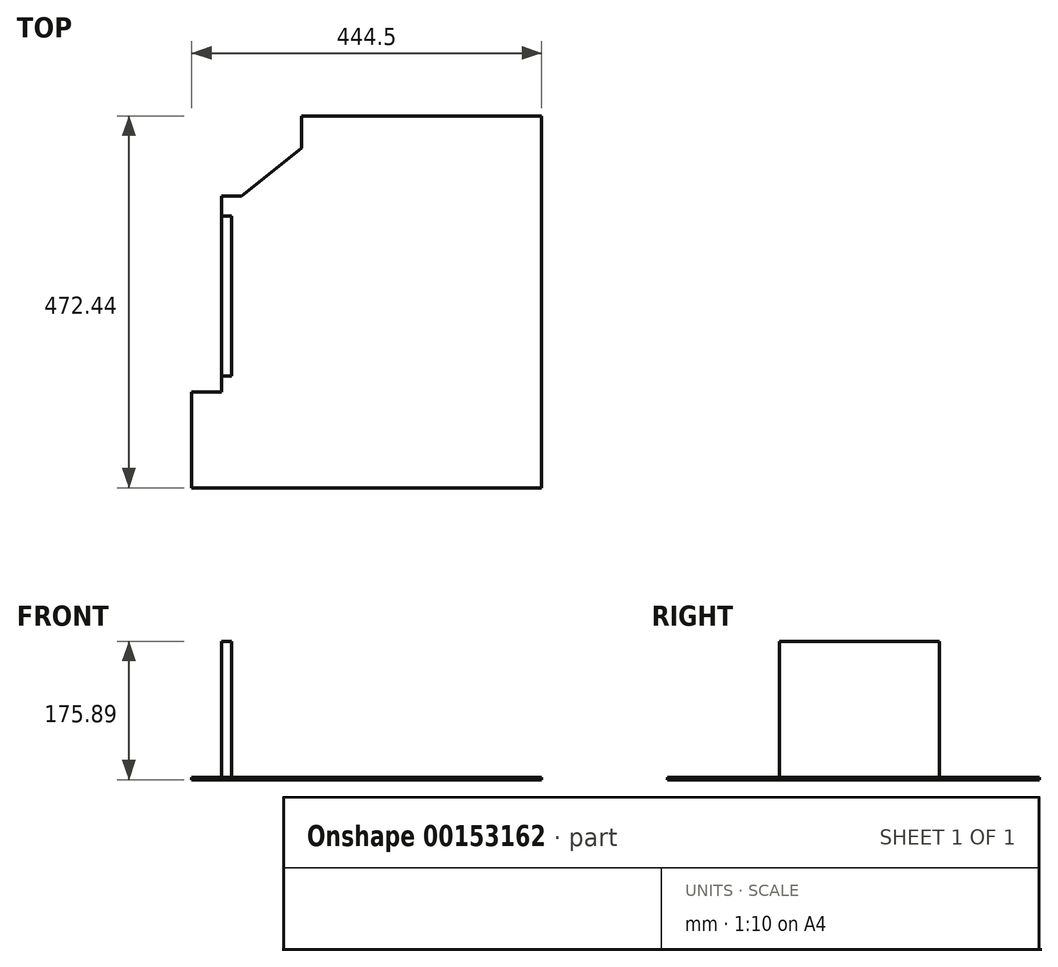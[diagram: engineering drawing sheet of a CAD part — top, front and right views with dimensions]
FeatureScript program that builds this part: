
annotation { "Feature Type Name" : "Feature", "Feature Type Description" : "" }
export const myFeature = defineFeature(function(context is Context, id is Id, definition is map)
    precondition{}
    {
        {
            var Q0;
            Q0=qCreatedBy(makeId("Top.planeOp"),FACE);
            var sketch = newSketch(context, id + "F0", { "sketchPlane" : qUnion([Q0])});
            skLineSegment(sketch, "E0", {"start": v(196.15, -173.15) * mm, "end": v(196.15, 299.29) * mm});
            skLineSegment(sketch, "E1", {"start": v(196.15, 299.29) * mm, "end": v(-108.65, 299.29) * mm});
            skLineSegment(sketch, "E2", {"start": v(-108.65, 299.29) * mm, "end": v(-108.65, 258.65) * mm});
            skLineSegment(sketch, "E3", {"start": v(-108.65, 258.65) * mm, "end": v(-184.85, 197.37) * mm});
            skLineSegment(sketch, "E4", {"start": v(-184.85, 197.69) * mm, "end": v(-184.85, 197.37) * mm});
            skLineSegment(sketch, "E5", {"start": v(-184.85, 197.69) * mm, "end": v(-210.25, 197.69) * mm});
            skLineSegment(sketch, "E6", {"start": v(-210.25, 197.69) * mm, "end": v(-210.25, -173.15) * mm});
            skLineSegment(sketch, "E7", {"start": v(-210.25, -173.15) * mm, "end": v(196.15, -173.15) * mm});
            skLineSegment(sketch, "E8.bottom", {"start": v(-210.25, -173.15) * mm, "end": v(-248.35, -173.15) * mm});
            skLineSegment(sketch, "E8.top", {"start": v(-210.25, -51.23) * mm, "end": v(-248.35, -51.23) * mm});
            skLineSegment(sketch, "E8.left", {"start": v(-210.25, -173.15) * mm, "end": v(-210.25, -51.23) * mm});
            skLineSegment(sketch, "E8.right", {"start": v(-248.35, -173.15) * mm, "end": v(-248.35, -51.23) * mm});
            skLineSegment(sketch, "E9.bottom", {"start": v(-210.25, -28.53) * mm, "end": v(-197.55, -28.53) * mm});
            skLineSegment(sketch, "E9.top", {"start": v(-210.25, 149.27) * mm, "end": v(-197.55, 149.27) * mm});
            skLineSegment(sketch, "E9.left", {"start": v(-210.25, -28.53) * mm, "end": v(-210.25, 149.27) * mm});
            skLineSegment(sketch, "E9.right", {"start": v(-197.55, -28.53) * mm, "end": v(-197.55, 149.27) * mm});
            skSolve(sketch);
        }
        {
            var Q0;
            Q0 = qSketchRegion(id + "F0", true);
            extrude(context, id + "F1", {"entities" : qUnion([Q0]), "depth" : 3.17 * mm});
        }
        {
            var Q0;
            Q0=makeQuery(id+"F1.opExtrude","CAP_FACE",FACE,{"disambiguationData":[OSD([sQuery(id+"F0.wireOp",EDGE,"E0"),sQuery(id+"F0.wireOp",EDGE,"E1"),sQuery(id+"F0.wireOp",EDGE,"E2"),sQuery(id+"F0.wireOp",EDGE,"E3"),sQuery(id+"F0.wireOp",EDGE,"E4"),sQuery(id+"F0.wireOp",EDGE,"E5"),sQuery(id+"F0.wireOp",EDGE,"E6"),sQuery(id+"F0.wireOp",EDGE,"E7"),sQuery(id+"F0.wireOp",EDGE,"E8.bottom"),sQuery(id+"F0.wireOp",EDGE,"E8.top"),sQuery(id+"F0.wireOp",EDGE,"E8.right"),sQuery(id+"F0.wireOp",EDGE,"E9.left")])],"isStart":false});
            var sketch = newSketch(context, id + "F2", { "sketchPlane" : qUnion([Q0])});
            skLineSegment(sketch, "E10.bottom", {"start": v(-210.25, -31.2) * mm, "end": v(-197.55, -31.2) * mm});
            skLineSegment(sketch, "E10.top", {"start": v(-210.25, 172.29) * mm, "end": v(-197.55, 172.29) * mm});
            skLineSegment(sketch, "E10.left", {"start": v(-210.25, -31.2) * mm, "end": v(-210.25, 172.29) * mm});
            skLineSegment(sketch, "E10.right", {"start": v(-197.55, -31.2) * mm, "end": v(-197.55, 172.29) * mm});
            skLineSegment(sketch, "E11.0", {"start": v(-184.85, 228.93) * mm, "end": v(-210.25, 228.93) * mm});
            skLineSegment(sketch, "E12.0", {"start": v(-115, 305.64) * mm, "end": v(-115, 261.7) * mm});
            skLineSegment(sketch, "E12.1", {"start": v(202.5, 305.64) * mm, "end": v(-115, 305.64) * mm});
            skLineSegment(sketch, "E12.2", {"start": v(-115, 261.7) * mm, "end": v(-186.69, 204.04) * mm});
            skLineSegment(sketch, "E12.3", {"start": v(202.5, -179.5) * mm, "end": v(202.5, 305.64) * mm});
            skLineSegment(sketch, "E12.4", {"start": v(202.5, -179.5) * mm, "end": v(-254.7, -179.5) * mm});
            skLineSegment(sketch, "E12.5", {"start": v(-186.69, 204.04) * mm, "end": v(-216.6, 204.04) * mm});
            skLineSegment(sketch, "E12.6", {"start": v(-216.6, -44.88) * mm, "end": v(-216.6, 204.04) * mm});
            skLineSegment(sketch, "E12.7", {"start": v(-216.6, -44.88) * mm, "end": v(-254.7, -44.88) * mm});
            skLineSegment(sketch, "E12.8", {"start": v(-254.7, -179.5) * mm, "end": v(-254.7, -44.88) * mm});
            skSolve(sketch);
        }
        {
            var Q0;
            {var subQ2=sQuery(id+"F2.wireOp",EDGE,"E10.left");Q0=makeQuery(id+"F2.imprint","IMPRINT",FACE,{"disambiguationData":[TD([[makeQuery(id+"F2.imprint","IMPRINT",EDGE,{"derivedFrom":subQ2}),1.0]])]});}
            extrude(context, id + "F3", {"entities" : qUnion([Q0]), "depth" : 172.72 * mm});
        }
    });
